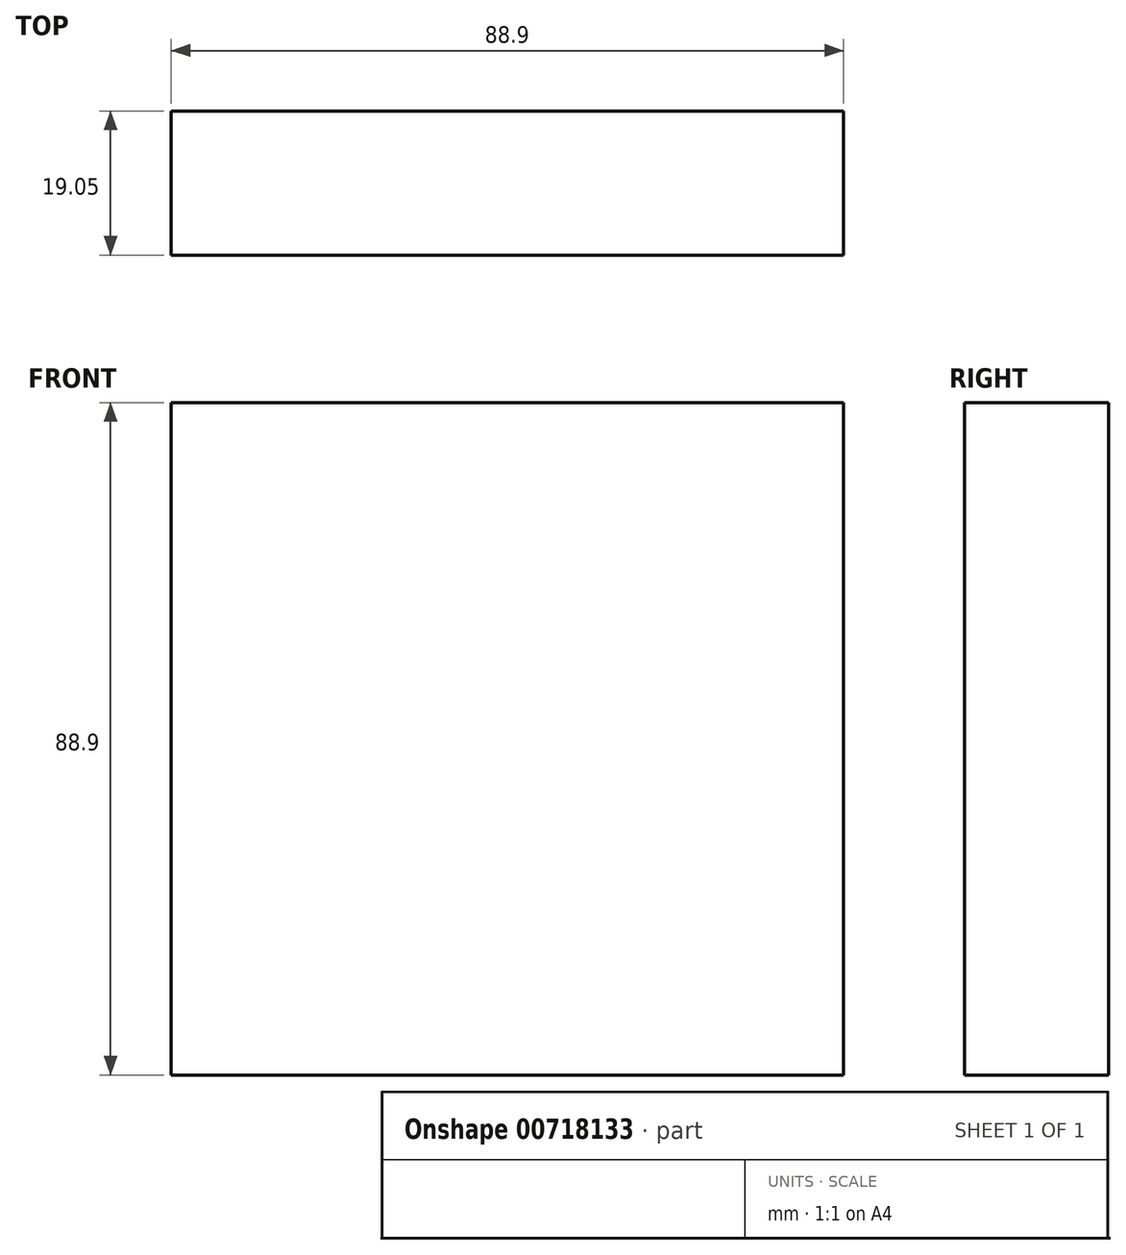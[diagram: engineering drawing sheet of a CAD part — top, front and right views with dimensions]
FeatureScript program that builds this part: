
annotation { "Feature Type Name" : "Feature", "Feature Type Description" : "" }
export const myFeature = defineFeature(function(context is Context, id is Id, definition is map)
    precondition{}
    {
        {
            var Q0;
            Q0=qCreatedBy(makeId("Front.planeOp"),FACE);
            var sketch = newSketch(context, id + "F0", { "sketchPlane" : qUnion([Q0])});
            skLineSegment(sketch, "E0.bottom", {"start": v(0, 0) * mm, "end": v(88.9, 0) * mm});
            skLineSegment(sketch, "E0.top", {"start": v(0, 88.9) * mm, "end": v(88.9, 88.9) * mm});
            skLineSegment(sketch, "E0.left", {"start": v(0, 0) * mm, "end": v(0, 88.9) * mm});
            skLineSegment(sketch, "E0.right", {"start": v(88.9, 0) * mm, "end": v(88.9, 88.9) * mm});
            skSolve(sketch);
        }
        {
            var Q0;
            Q0=makeQuery(id+"F0.imprint","IMPRINT",FACE,{"disambiguationData":[TD([[makeQuery(id+"F0.imprint","IMPRINT",EDGE,{"derivedFrom":sQuery(id+"F0.wireOp",EDGE,"E0.bottom")}),1.0]])]});
            extrude(context, id + "F1", {"entities" : qUnion([Q0]), "depth" : 19.05 * mm, "offsetDistance" : 25.4 * mm});
        }
    });
